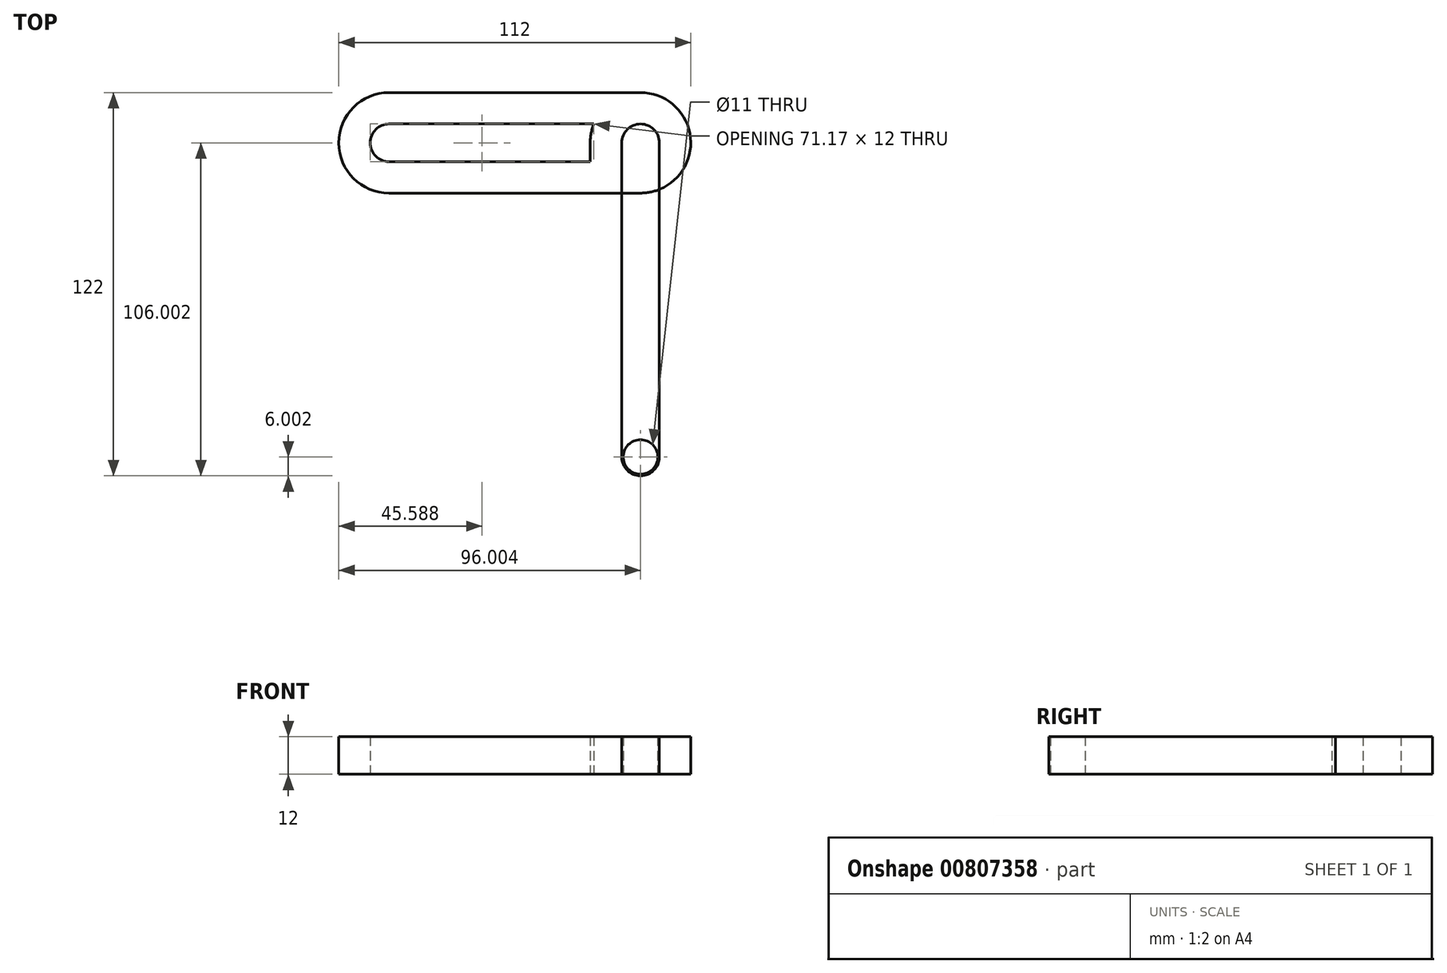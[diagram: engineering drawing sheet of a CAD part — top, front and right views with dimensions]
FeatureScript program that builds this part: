
annotation { "Feature Type Name" : "Feature", "Feature Type Description" : "" }
export const myFeature = defineFeature(function(context is Context, id is Id, definition is map)
    precondition{}
    {
        {
            var Q0;
            Q0=qCreatedBy(makeId("Top.planeOp"),FACE);
            var sketch = newSketch(context, id + "F0", { "sketchPlane" : qUnion([Q0])});
            skLineSegment(sketch, "E0", {"start": v(-46.66, 48) * mm, "end": v(33.34, 48) * mm});
            skLineSegment(sketch, "E1", {"start": v(-46.66, 16) * mm, "end": v(33.34, 16) * mm});
            skArc(sketch, "E2", {"start": v(33.34, 48) * mm, "mid": v(49.34, 32) * mm, "end": v(33.34, 16) * mm});
            skArc(sketch, "E3", {"start": v(-46.66, 48) * mm, "mid": v(-62.66, 32) * mm, "end": v(-46.66, 16) * mm});
            skArc(sketch, "E4.0", {"start": v(-46.66, 38) * mm, "mid": v(-52.66, 32) * mm, "end": v(-46.66, 26) * mm});
            skLineSegment(sketch, "E4.1", {"start": v(-46.66, 38) * mm, "end": v(33.34, 38) * mm});
            skArc(sketch, "E4.2", {"start": v(33.34, 38) * mm, "mid": v(39.34, 32) * mm, "end": v(33.34, 26) * mm});
            skLineSegment(sketch, "E4.3", {"start": v(-46.66, 26) * mm, "end": v(33.34, 26) * mm});
            skCircle(sketch, "E5", {"center": v(33.34, 32) * mm, "radius": 5.5 * mm});
            skCircle(sketch, "E6", {"center": v(-46.66, 32) * mm, "radius": 5.5 * mm});
            skLineSegment(sketch, "E7", {"start": v(39.34, 32) * mm, "end": v(39.34, -68) * mm});
            skPoint(sketch, "E7.endSnap0", {"position": v(39.34, 32) * mm});
            skLineSegment(sketch, "E8", {"start": v(27.34, 32) * mm, "end": v(27.34, -68) * mm});
            skArc(sketch, "E9", {"start": v(27.34, 32) * mm, "mid": v(33.34, 38) * mm, "end": v(39.34, 32) * mm});
            skArc(sketch, "E10", {"start": v(39.34, -68) * mm, "mid": v(33.34, -74) * mm, "end": v(27.34, -68) * mm});
            skLineSegment(sketch, "E11.0", {"start": v(49.34, 32) * mm, "end": v(49.34, -68) * mm});
            skArc(sketch, "E11.1", {"start": v(17.34, 32) * mm, "mid": v(33.34, 48) * mm, "end": v(49.34, 32) * mm});
            skLineSegment(sketch, "E11.2", {"start": v(17.34, 32) * mm, "end": v(17.34, -68) * mm});
            skArc(sketch, "E11.3", {"start": v(49.34, -68) * mm, "mid": v(33.34, -84) * mm, "end": v(17.34, -68) * mm});
            skCircle(sketch, "E12", {"center": v(33.34, -68) * mm, "radius": 5.5 * mm});
            skSolve(sketch);
        }
        {
            var Q0;
            {var subQ0=sQuery(id+"F0.wireOp",EDGE,"E9");var subQ1=sQuery(id+"F0.wireOp",EDGE,"E4.1");var subQ2=makeQuery(id+"F0.imprint","INTERSECT",VERTEX,{"derivedFrom":[subQ1,subQ0]});Q0=makeQuery(id+"F0.imprint","IMPRINT",FACE,{"disambiguationData":[TD([[makeQuery(id+"F0.imprint","IMPRINT",EDGE,{"disambiguationData":[TD([[subQ2,1.0]])],"derivedFrom":subQ1}),1.0]])]});}
            var Q1;
            {var subQ0=sQuery(id+"F0.wireOp",EDGE,"E10");Q1=makeQuery(id+"F0.imprint","IMPRINT",FACE,{"disambiguationData":[TD([[makeQuery(id+"F0.imprint","IMPRINT",EDGE,{"derivedFrom":subQ0}),1.0]])]});}
            var Q2;
            {var subQ0=sQuery(id+"F0.wireOp",EDGE,"E9");var subQ1=sQuery(id+"F0.wireOp",EDGE,"E4.1");var subQ2=makeQuery(id+"F0.imprint","INTERSECT",VERTEX,{"derivedFrom":[subQ1,subQ0]});Q2=makeQuery(id+"F0.imprint","IMPRINT",FACE,{"disambiguationData":[TD([[makeQuery(id+"F0.imprint","IMPRINT",EDGE,{"disambiguationData":[TD([[subQ2,1.0]])],"derivedFrom":subQ1}),-1.0]])]});}
            var Q3;
            {var subQ0=sQuery(id+"F0.wireOp",EDGE,"E11.2");var subQ1=sQuery(id+"F0.wireOp",EDGE,"E1");var subQ2=makeQuery(id+"F0.imprint","INTERSECT",VERTEX,{"derivedFrom":[subQ1,subQ0]});Q3=makeQuery(id+"F0.imprint","IMPRINT",FACE,{"disambiguationData":[TD([[makeQuery(id+"F0.imprint","IMPRINT",EDGE,{"disambiguationData":[TD([[subQ2,-1.0]])],"derivedFrom":subQ1}),1.0]])]});}
            var Q4;
            {var subQ7=sQuery(id+"F0.wireOp",EDGE,"E0");Q4=makeQuery(id+"F0.imprint","IMPRINT",FACE,{"disambiguationData":[TD([[makeQuery(id+"F0.imprint","IMPRINT",EDGE,{"derivedFrom":subQ7}),-1.0]])]});}
            extrude(context, id + "F1", {"entities" : qUnion([Q0, Q1, Q2, Q3, Q4]), "depth" : 12 * mm, "offsetDistance" : 25.4 * mm});
        }
    });
